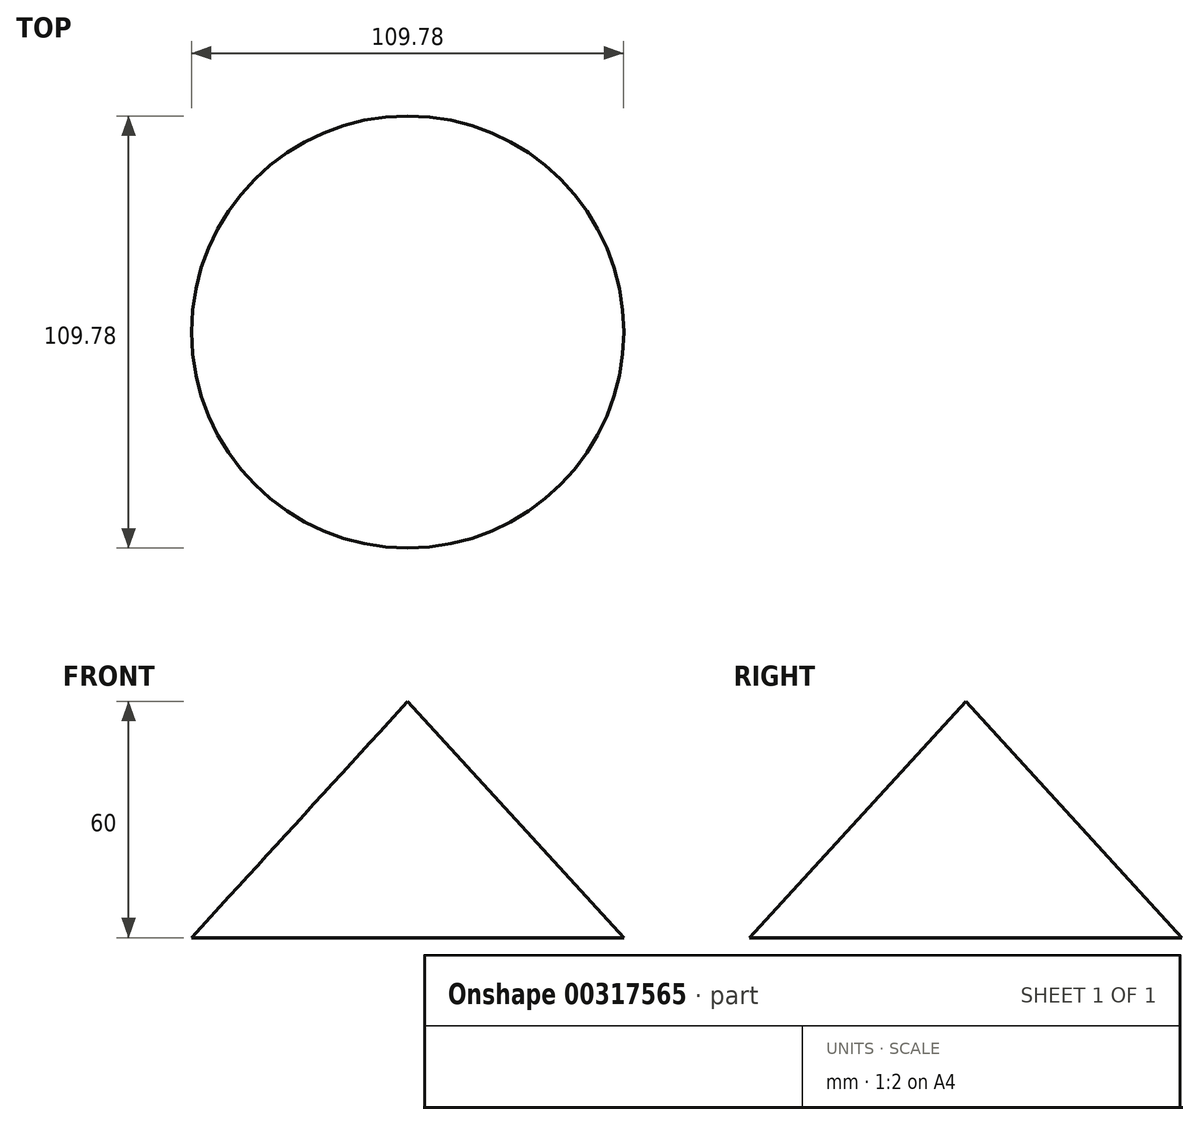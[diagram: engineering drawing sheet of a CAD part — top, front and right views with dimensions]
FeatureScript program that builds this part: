
annotation { "Feature Type Name" : "Feature", "Feature Type Description" : "" }
export const myFeature = defineFeature(function(context is Context, id is Id, definition is map)
    precondition{}
    {
        {
            var Q0;
            Q0=qCreatedBy(makeId("Front.planeOp"),FACE);
            var sketch = newSketch(context, id + "F0", { "sketchPlane" : qUnion([Q0])});
            skLineSegment(sketch, "E0", {"start": v(0, 0) * mm, "end": v(-54.9, 0) * mm});
            skLineSegment(sketch, "E1", {"start": v(-54.9, 0) * mm, "end": v(0, 60) * mm});
            skLineSegment(sketch, "E2", {"start": v(0, 60) * mm, "end": v(54.9, 0) * mm});
            skLineSegment(sketch, "E3", {"start": v(0, 0) * mm, "end": v(54.9, 0) * mm});
            skLineSegment(sketch, "E4", {"start": v(0, 60) * mm, "end": v(0, 0) * mm});
            skSolve(sketch);
        }
        {
            var Q0;
            Q0=makeQuery(id+"F0.imprint","IMPRINT",FACE,{"disambiguationData":[TD([[makeQuery(id+"F0.imprint","IMPRINT",EDGE,{"derivedFrom":sQuery(id+"F0.wireOp",EDGE,"E2")}),-1.0]])]});
            var Q1;
            Q1=sQuery(id+"F0.wireOp",EDGE,"E4");
            revolve(context, id + "F1", {"entities" : qUnion([Q0]), "axis" : qUnion([Q1]), "revolveType" : RevolveType.FULL, "oppositeDirection" : true});
        }
    });
